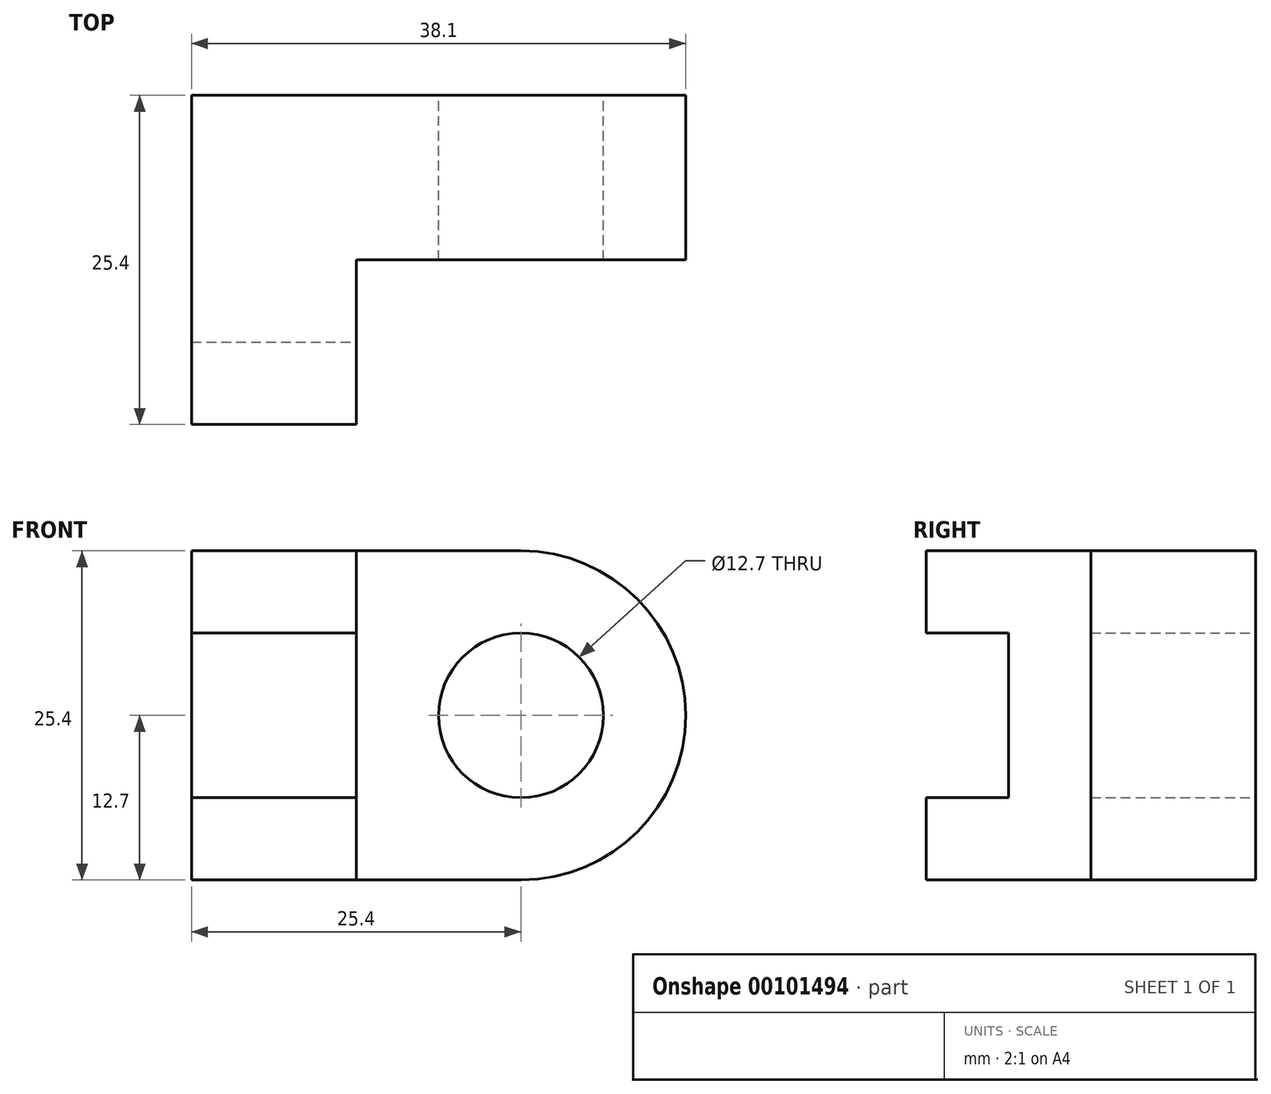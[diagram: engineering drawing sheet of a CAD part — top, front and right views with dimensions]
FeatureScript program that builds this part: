
annotation { "Feature Type Name" : "Feature", "Feature Type Description" : "" }
export const myFeature = defineFeature(function(context is Context, id is Id, definition is map)
    precondition{}
    {
        {
            var Q0;
            Q0=qCreatedBy(makeId("Front.planeOp"),FACE);
            var sketch = newSketch(context, id + "F0", { "sketchPlane" : qUnion([Q0])});
            skLineSegment(sketch, "E0", {"start": v(0, 0) * mm, "end": v(0, 25.4) * mm});
            skLineSegment(sketch, "E1", {"start": v(0, 25.4) * mm, "end": v(25.4, 25.4) * mm});
            skLineSegment(sketch, "E2", {"start": v(0, 0) * mm, "end": v(25.4, 0) * mm});
            skArc(sketch, "E3", {"start": v(25.4, 25.4) * mm, "mid": v(38.1, 12.7) * mm, "end": v(25.4, 0) * mm});
            skCircle(sketch, "E4", {"center": v(25.4, 12.7) * mm, "radius": 6.35 * mm});
            skSolve(sketch);
        }
        {
            var Q0;
            Q0=makeQuery(id+"F0.imprint","IMPRINT",FACE,{"disambiguationData":[TD([[makeQuery(id+"F0.imprint","IMPRINT",EDGE,{"derivedFrom":sQuery(id+"F0.wireOp",EDGE,"E0")}),-1.0]])]});
            extrude(context, id + "F1", {"entities" : qUnion([Q0]), "depth" : 12.7 * mm});
        }
        {
            var Q0;
            Q0=makeQuery(id+"F1.opExtrude","CAP_FACE",FACE,{"disambiguationData":[OSD([sQuery(id+"F0.wireOp",EDGE,"E0"),sQuery(id+"F0.wireOp",EDGE,"E1"),sQuery(id+"F0.wireOp",EDGE,"E2"),sQuery(id+"F0.wireOp",EDGE,"E3"),sQuery(id+"F0.wireOp",EDGE,"E4")])],"isStart":false});
            var sketch = newSketch(context, id + "F2", { "sketchPlane" : qUnion([Q0])});
            skLineSegment(sketch, "E5", {"start": v(12.7, 0) * mm, "end": v(12.7, 25.4) * mm});
            skSolve(sketch);
        }
        {
            var Q0;
            {var subQ0=sQuery(id+"F2.wireOp",EDGE,"E5");Q0=makeQuery(id+"F2.imprint","IMPRINT",FACE,{"disambiguationData":[TD([[makeQuery(id+"F2.imprint","IMPRINT",EDGE,{"derivedFrom":subQ0}),1.0]])]});}
            extrude(context, id + "F3", {"entities" : qUnion([Q0]), "operationType" : NewBodyOperationType.ADD, "depth" : 12.7 * mm});
        }
        {
            var Q0;
            Q0=makeQuery(id+"F3.opExtrude","SWEPT_FACE",FACE,{"disambiguationData":[OSD([sQuery(id+"F2.wireOp",EDGE,"E5")])]});
            var sketch = newSketch(context, id + "F4", { "sketchPlane" : qUnion([Q0])});
            skLineSegment(sketch, "E6", {"start": v(-25.4, 19.05) * mm, "end": v(-19.05, 19.05) * mm});
            skLineSegment(sketch, "E7", {"start": v(-19.05, 19.05) * mm, "end": v(-19.05, 6.35) * mm});
            skLineSegment(sketch, "E8", {"start": v(-19.05, 6.35) * mm, "end": v(-25.4, 6.35) * mm});
            skSolve(sketch);
        }
        {
            var Q0;
            {var subQ0=sQuery(id+"F4.wireOp",EDGE,"E6");Q0=makeQuery(id+"F4.imprint","IMPRINT",FACE,{"disambiguationData":[TD([[makeQuery(id+"F4.imprint","IMPRINT",EDGE,{"derivedFrom":subQ0}),-1.0]])]});}
            extrude(context, id + "F5", {"entities" : qUnion([Q0]), "operationType" : NewBodyOperationType.REMOVE, "endBound" : BoundingType.THROUGH_ALL, "oppositeDirection" : true, "depth" : 25.4 * mm});
        }
    });
